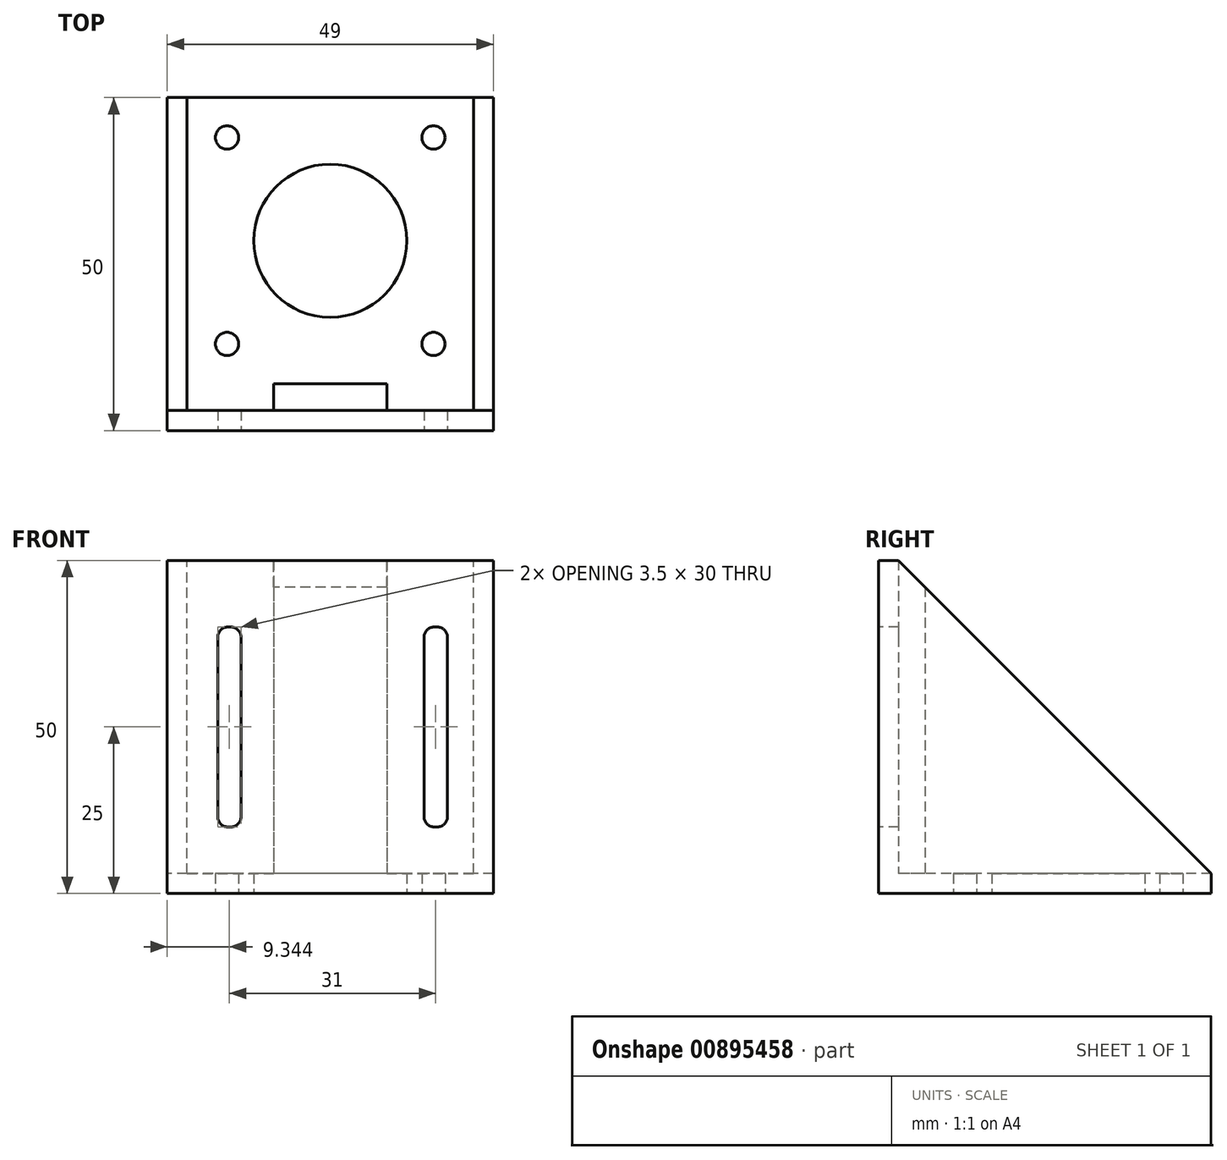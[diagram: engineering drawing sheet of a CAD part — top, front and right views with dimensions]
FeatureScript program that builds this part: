
annotation { "Feature Type Name" : "Feature", "Feature Type Description" : "" }
export const myFeature = defineFeature(function(context is Context, id is Id, definition is map)
    precondition{}
    {
        {
            var Q0;
            Q0=qCreatedBy(makeId("Top.planeOp"),FACE);
            var sketch = newSketch(context, id + "F0", { "sketchPlane" : qUnion([Q0])});
            skLineSegment(sketch, "E0.bottom", {"start": v(21.5, 21.5) * mm, "end": v(-21.5, 21.5) * mm});
            skLineSegment(sketch, "E0.top", {"start": v(21.5, -21.5) * mm, "end": v(-21.5, -21.5) * mm});
            skLineSegment(sketch, "E0.left", {"start": v(21.5, 21.5) * mm, "end": v(21.5, -21.5) * mm});
            skLineSegment(sketch, "E0.right", {"start": v(-21.5, 21.5) * mm, "end": v(-21.5, -21.5) * mm});
            skPoint(sketch, "E0.middle", {"position": v(0, 0) * mm});
            skCircle(sketch, "E1", {"center": v(0, 0) * mm, "radius": 11.5 * mm});
            skCircle(sketch, "E2", {"center": v(15.5, 15.5) * mm, "radius": 1.75 * mm});
            skCircle(sketch, "E3.0.1.0", {"center": v(15.5, -15.5) * mm, "radius": 1.75 * mm});
            skCircle(sketch, "E3.1.0.0", {"center": v(-15.5, 15.5) * mm, "radius": 1.75 * mm});
            skCircle(sketch, "E3.1.1.0", {"center": v(-15.5, -15.5) * mm, "radius": 1.75 * mm});
            skLineSegment(sketch, "E3.direction1", {"start": v(15.5, 15.5) * mm, "end": v(-15.5, 15.5) * mm, "construction": true});
            skLineSegment(sketch, "E3.direction2", {"start": v(15.5, 15.5) * mm, "end": v(15.5, -15.5) * mm, "construction": true});
            skLineSegment(sketch, "E4.top", {"start": v(-24.5, -28.5) * mm, "end": v(24.5, -28.5) * mm});
            skLineSegment(sketch, "E5.top", {"start": v(-24.5, -25.5) * mm, "end": v(24.5, -25.5) * mm});
            skLineSegment(sketch, "E5.left", {"start": v(-24.5, -28.5) * mm, "end": v(-24.5, -25.5) * mm});
            skLineSegment(sketch, "E5.right", {"start": v(24.5, -28.5) * mm, "end": v(24.5, -25.5) * mm});
            skLineSegment(sketch, "E6", {"start": v(-8.5, -21.5) * mm, "end": v(-8.5, -25.5) * mm});
            skLineSegment(sketch, "E7", {"start": v(8.5, -21.5) * mm, "end": v(8.5, -25.5) * mm});
            skLineSegment(sketch, "E8.bottom", {"start": v(-24.5, -25.5) * mm, "end": v(-21.5, -25.5) * mm});
            skLineSegment(sketch, "E8.top", {"start": v(-24.5, 21.5) * mm, "end": v(-21.5, 21.5) * mm});
            skLineSegment(sketch, "E8.left", {"start": v(-24.5, -25.5) * mm, "end": v(-24.5, 21.5) * mm});
            skLineSegment(sketch, "E8.right", {"start": v(-21.5, -25.5) * mm, "end": v(-21.5, 21.5) * mm});
            skLineSegment(sketch, "E9.bottom", {"start": v(21.5, 21.5) * mm, "end": v(24.5, 21.5) * mm});
            skLineSegment(sketch, "E9.top", {"start": v(21.5, -25.5) * mm, "end": v(24.5, -25.5) * mm});
            skLineSegment(sketch, "E9.left", {"start": v(21.5, 21.5) * mm, "end": v(21.5, -25.5) * mm});
            skLineSegment(sketch, "E9.right", {"start": v(24.5, 21.5) * mm, "end": v(24.5, -25.5) * mm});
            skSolve(sketch);
        }
        {
            var Q0;
            Q0=makeQuery(id+"F0.imprint","IMPRINT",FACE,{"disambiguationData":[TD([[makeQuery(id+"F0.imprint","IMPRINT",EDGE,{"derivedFrom":sQuery(id+"F0.wireOp",EDGE,"E0.right")}),-1.0]])]});
            var Q1;
            Q1=makeQuery(id+"F0.imprint","IMPRINT",FACE,{"disambiguationData":[TD([[makeQuery(id+"F0.imprint","IMPRINT",EDGE,{"derivedFrom":sQuery(id+"F0.wireOp",EDGE,"E4.top")}),1.0]])]});
            var Q2;
            Q2=makeQuery(id+"F0.imprint","IMPRINT",FACE,{"disambiguationData":[TD([[makeQuery(id+"F0.imprint","IMPRINT",EDGE,{"derivedFrom":sQuery(id+"F0.wireOp",EDGE,"E0.left")}),1.0]])]});
            var Q3;
            {var subQ2=sQuery(id+"F0.wireOp",EDGE,"E6");Q3=makeQuery(id+"F0.imprint","IMPRINT",FACE,{"disambiguationData":[TD([[makeQuery(id+"F0.imprint","IMPRINT",EDGE,{"derivedFrom":subQ2}),1.0]])]});}
            extrude(context, id + "F1", {"entities" : qUnion([Q0, Q1, Q2, Q3]), "depth" : 50 * mm, "offsetDistance" : 25 * mm});
        }
        {
            var Q0;
            Q0=makeQuery(id+"F0.imprint","IMPRINT",FACE,{"disambiguationData":[TD([[makeQuery(id+"F0.imprint","IMPRINT",EDGE,{"derivedFrom":sQuery(id+"F0.wireOp",EDGE,"E0.bottom")}),1.0]])]});
            var Q1;
            {var subQ0=sQuery(id+"F0.wireOp",EDGE,"E7");Q1=makeQuery(id+"F0.imprint","IMPRINT",FACE,{"disambiguationData":[TD([[makeQuery(id+"F0.imprint","IMPRINT",EDGE,{"derivedFrom":subQ0}),1.0]])]});}
            var Q2;
            {var subQ2=sQuery(id+"F0.wireOp",EDGE,"E6");Q2=makeQuery(id+"F0.imprint","IMPRINT",FACE,{"disambiguationData":[TD([[makeQuery(id+"F0.imprint","IMPRINT",EDGE,{"derivedFrom":subQ2}),-1.0]])]});}
            extrude(context, id + "F2", {"entities" : qUnion([Q0, Q1, Q2]), "operationType" : NewBodyOperationType.ADD, "depth" : 3 * mm, "offsetDistance" : 25 * mm});
        }
        {
            var Q0;
            Q0=makeQuery(id+"F1.opExtrude","SWEPT_FACE",FACE,{"disambiguationData":[OSD([sQuery(id+"F0.wireOp",EDGE,"E0.left"),sQuery(id+"F0.wireOp",EDGE,"E9.left")])]});
            var sketch = newSketch(context, id + "F3", { "sketchPlane" : qUnion([Q0])});
            skLineSegment(sketch, "E10", {"start": v(25.5, 50) * mm, "end": v(-21.5, 3) * mm});
            skLineSegment(sketch, "E11", {"start": v(-21.5, 3) * mm, "end": v(-21.5, 50) * mm});
            skLineSegment(sketch, "E12", {"start": v(-21.5, 50) * mm, "end": v(25.5, 50) * mm});
            skSolve(sketch);
        }
        {
            var Q0;
            Q0=makeQuery(id+"F3.imprint","IMPRINT",FACE,{"disambiguationData":[TD([[makeQuery(id+"F3.imprint","IMPRINT",EDGE,{"derivedFrom":sQuery(id+"F3.wireOp",EDGE,"E10")}),-1.0]])]});
            extrude(context, id + "F4", {"entities" : qUnion([Q0]), "operationType" : NewBodyOperationType.REMOVE, "oppositeDirection" : true, "depth" : 5 * mm, "offsetDistance" : 25 * mm, "hasSecondDirection" : true, "secondDirectionOppositeDirection" : false, "secondDirectionDepth" : 50 * mm});
        }
        {
            var Q0;
            Q0=makeQuery(id+"F1.opExtrude","SWEPT_FACE",FACE,{"disambiguationData":[OSD([sQuery(id+"F0.wireOp",EDGE,"E4.top")])]});
            var sketch = newSketch(context, id + "F5", { "sketchPlane" : qUnion([Q0])});
            skLineSegment(sketch, "E13.bottom", {"start": v(16.1, 40) * mm, "end": v(15.6, 40) * mm});
            skLineSegment(sketch, "E13.top", {"start": v(16.1, 10) * mm, "end": v(15.6, 10) * mm});
            skLineSegment(sketch, "E13.left", {"start": v(17.6, 38.5) * mm, "end": v(17.6, 11.5) * mm});
            skLineSegment(sketch, "E13.right", {"start": v(14.1, 38.5) * mm, "end": v(14.1, 11.5) * mm});
            skPoint(sketch, "E13.middle", {"position": v(15.84, 25) * mm});
            skPoint(sketch, "E14.visualSharp", {"position": v(17.6, 40) * mm});
            skArc(sketch, "E14.filletArc", {"start": v(17.6, 38.5) * mm, "mid": v(17.16, 39.56) * mm, "end": v(16.1, 40) * mm});
            skPoint(sketch, "E15.visualSharp", {"position": v(14.1, 40) * mm});
            skArc(sketch, "E15.filletArc", {"start": v(15.6, 40) * mm, "mid": v(14.53, 39.56) * mm, "end": v(14.1, 38.5) * mm});
            skPoint(sketch, "E16.visualSharp", {"position": v(14.1, 10) * mm});
            skArc(sketch, "E16.filletArc", {"start": v(14.1, 11.5) * mm, "mid": v(14.53, 10.44) * mm, "end": v(15.6, 10) * mm});
            skPoint(sketch, "E17.visualSharp", {"position": v(17.6, 10) * mm});
            skArc(sketch, "E17.filletArc", {"start": v(16.1, 10) * mm, "mid": v(17.16, 10.44) * mm, "end": v(17.6, 11.5) * mm});
            skLineSegment(sketch, "E18.1.0.0", {"start": v(-13.4, 38.5) * mm, "end": v(-13.4, 11.5) * mm});
            skPoint(sketch, "E18.1.0.1", {"position": v(-13.4, 40) * mm});
            skLineSegment(sketch, "E18.1.0.2", {"start": v(-16.9, 38.5) * mm, "end": v(-16.9, 11.5) * mm});
            skPoint(sketch, "E18.1.0.3", {"position": v(-15.16, 25) * mm});
            skPoint(sketch, "E18.1.0.4", {"position": v(-13.4, 10) * mm});
            skPoint(sketch, "E18.1.0.5", {"position": v(-16.9, 40) * mm});
            skPoint(sketch, "E18.1.0.6", {"position": v(-16.9, 10) * mm});
            skArc(sketch, "E18.1.0.7", {"start": v(-13.4, 38.5) * mm, "mid": v(-13.84, 39.56) * mm, "end": v(-14.9, 40) * mm});
            skArc(sketch, "E18.1.0.8", {"start": v(-16.9, 11.5) * mm, "mid": v(-16.47, 10.44) * mm, "end": v(-15.4, 10) * mm});
            skArc(sketch, "E18.1.0.9", {"start": v(-15.4, 40) * mm, "mid": v(-16.47, 39.56) * mm, "end": v(-16.9, 38.5) * mm});
            skArc(sketch, "E18.1.0.10", {"start": v(-14.9, 10) * mm, "mid": v(-13.84, 10.44) * mm, "end": v(-13.4, 11.5) * mm});
            skLineSegment(sketch, "E18.1.0.11", {"start": v(-14.9, 40) * mm, "end": v(-15.4, 40) * mm});
            skLineSegment(sketch, "E18.1.0.12", {"start": v(-14.9, 10) * mm, "end": v(-15.4, 10) * mm});
            skLineSegment(sketch, "E18.direction1", {"start": v(14.1, 10) * mm, "end": v(-16.9, 10) * mm, "construction": true});
            skSolve(sketch);
        }
        {
            var Q0;
            Q0=makeQuery(id+"F5.imprint","IMPRINT",FACE,{"disambiguationData":[TD([[makeQuery(id+"F5.imprint","IMPRINT",EDGE,{"derivedFrom":sQuery(id+"F5.wireOp",EDGE,"E13.bottom")}),1.0]])]});
            var Q1;
            Q1=makeQuery(id+"F5.imprint","IMPRINT",FACE,{"disambiguationData":[TD([[makeQuery(id+"F5.imprint","IMPRINT",EDGE,{"derivedFrom":sQuery(id+"F5.wireOp",EDGE,"E18.1.0.0")}),-1.0]])]});
            extrude(context, id + "F6", {"entities" : qUnion([Q0, Q1]), "operationType" : NewBodyOperationType.REMOVE, "oppositeDirection" : true, "depth" : 3 * mm, "offsetDistance" : 25 * mm});
        }
    });
